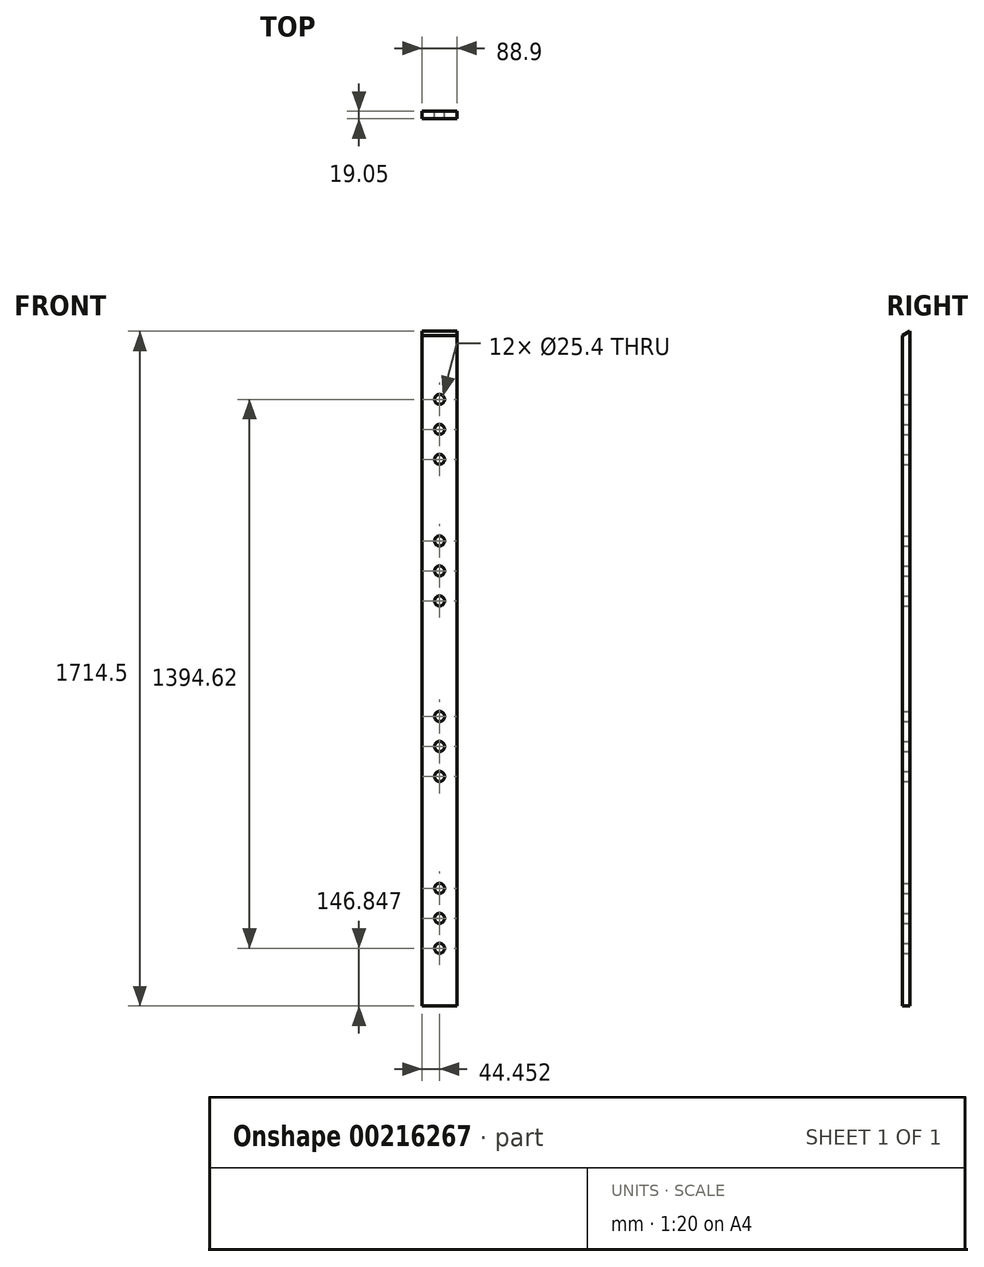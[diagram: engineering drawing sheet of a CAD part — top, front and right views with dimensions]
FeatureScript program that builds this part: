
annotation { "Feature Type Name" : "Feature", "Feature Type Description" : "" }
export const myFeature = defineFeature(function(context is Context, id is Id, definition is map)
    precondition{}
    {
        {
            var Q0;
            Q0=qCreatedBy(makeId("Front.planeOp"),FACE);
            var sketch = newSketch(context, id + "F0", { "sketchPlane" : qUnion([Q0])});
            skLineSegment(sketch, "E0", {"start": v(-2057.27, 202.03) * mm, "end": v(-2057.27, -1513.2) * mm});
            skLineSegment(sketch, "E1", {"start": v(-2057.27, -1512.47) * mm, "end": v(-1968.37, -1512.47) * mm});
            skLineSegment(sketch, "E2", {"start": v(-1968.37, -1512.47) * mm, "end": v(-1968.37, 202.03) * mm});
            skLineSegment(sketch, "E3", {"start": v(-1968.37, 202.03) * mm, "end": v(-2057.27, 202.03) * mm});
            skCircle(sketch, "E4", {"center": v(-2012.82, 29) * mm, "radius": 12.7 * mm});
            skCircle(sketch, "E5", {"center": v(-2012.82, -47.2) * mm, "radius": 12.7 * mm});
            skCircle(sketch, "E6", {"center": v(-2012.82, -123.4) * mm, "radius": 12.7 * mm});
            skCircle(sketch, "E7", {"center": v(-2012.82, -330.57) * mm, "radius": 12.7 * mm});
            skCircle(sketch, "E8", {"center": v(-2012.82, -406.77) * mm, "radius": 12.7 * mm});
            skCircle(sketch, "E9", {"center": v(-2012.82, -482.97) * mm, "radius": 12.7 * mm});
            skCircle(sketch, "E10", {"center": v(-2012.82, -776.66) * mm, "radius": 12.7 * mm});
            skCircle(sketch, "E11", {"center": v(-2012.82, -852.86) * mm, "radius": 12.7 * mm});
            skCircle(sketch, "E12", {"center": v(-2012.82, -929.06) * mm, "radius": 12.7 * mm});
            skCircle(sketch, "E13", {"center": v(-2012.82, -1213.22) * mm, "radius": 12.7 * mm});
            skCircle(sketch, "E14", {"center": v(-2012.82, -1289.42) * mm, "radius": 12.7 * mm});
            skCircle(sketch, "E15", {"center": v(-2012.82, -1365.62) * mm, "radius": 12.7 * mm});
            skLineSegment(sketch, "E16", {"start": v(-2012.82, -1513.2) * mm, "end": v(-2012.82, 202.03) * mm, "construction": true});
            skSolve(sketch);
        }
        {
            var Q0;
            Q0=makeQuery(id+"F0.imprint","IMPRINT",FACE,{"disambiguationData":[TD([[makeQuery(id+"F0.imprint","IMPRINT",EDGE,{"derivedFrom":sQuery(id+"F0.wireOp",EDGE,"E0")}),1.0]])]});
            extrude(context, id + "F1", {"entities" : qUnion([Q0]), "depth" : 19.05 * mm});
        }
        {
            var Q0;
            Q0=makeQuery(id+"F1.opExtrude","SWEPT_FACE",FACE,{"disambiguationData":[OSD([sQuery(id+"F0.wireOp",EDGE,"E2")])]});
            var sketch = newSketch(context, id + "F2", { "sketchPlane" : qUnion([Q0])});
            skLineSegment(sketch, "E17", {"start": v(0, 202.03) * mm, "end": v(-19.05, 191.59) * mm});
            skLineSegment(sketch, "E18", {"start": v(-19.05, 191.59) * mm, "end": v(-19.05, 202.03) * mm});
            skLineSegment(sketch, "E19", {"start": v(-19.05, 202.03) * mm, "end": v(0, 202.03) * mm});
            skSolve(sketch);
        }
        {
            var Q0;
            Q0=makeQuery(id+"F2.imprint","IMPRINT",FACE,{"disambiguationData":[TD([[makeQuery(id+"F2.imprint","IMPRINT",EDGE,{"derivedFrom":sQuery(id+"F2.wireOp",EDGE,"E17")}),-1.0]])]});
            extrude(context, id + "F3", {"entities" : qUnion([Q0]), "operationType" : NewBodyOperationType.REMOVE, "endBound" : BoundingType.THROUGH_ALL, "oppositeDirection" : true, "depth" : 25.4 * mm});
        }
    });
